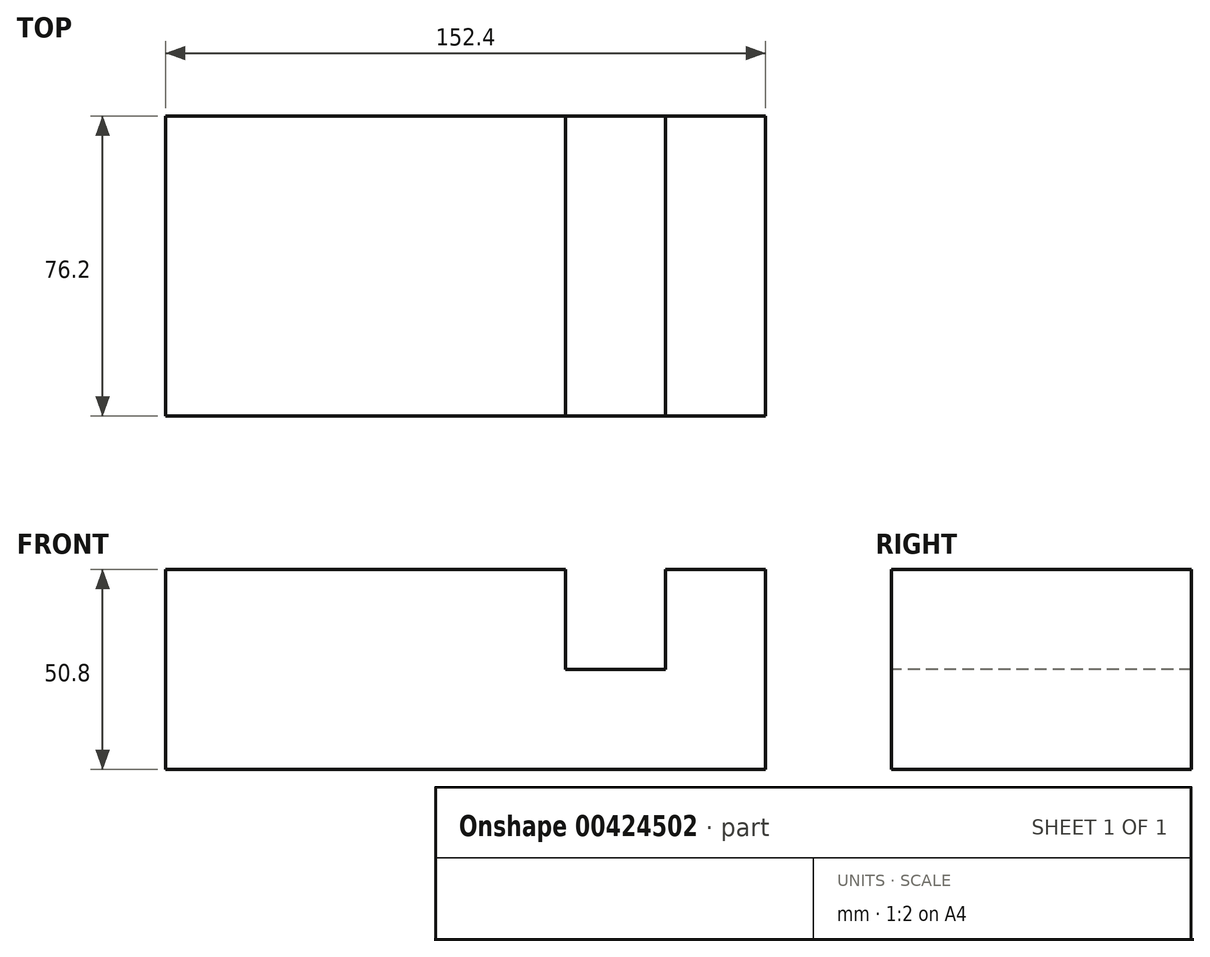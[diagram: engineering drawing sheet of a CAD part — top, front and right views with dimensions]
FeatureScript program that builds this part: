
annotation { "Feature Type Name" : "Feature", "Feature Type Description" : "" }
export const myFeature = defineFeature(function(context is Context, id is Id, definition is map)
    precondition{}
    {
        {
            var Q0;
            Q0=qCreatedBy(makeId("Front.planeOp"),FACE);
            var sketch = newSketch(context, id + "F0", { "sketchPlane" : qUnion([Q0])});
            skLineSegment(sketch, "E0", {"start": v(0, 0) * mm, "end": v(152.4, 0) * mm});
            skLineSegment(sketch, "E1", {"start": v(152.4, 0) * mm, "end": v(152.4, 50.8) * mm});
            skLineSegment(sketch, "E2", {"start": v(152.4, 50.8) * mm, "end": v(127, 50.8) * mm});
            skLineSegment(sketch, "E3", {"start": v(127, 50.8) * mm, "end": v(127, 25.4) * mm});
            skLineSegment(sketch, "E4", {"start": v(127, 25.4) * mm, "end": v(101.6, 25.4) * mm});
            skLineSegment(sketch, "E5", {"start": v(101.6, 25.4) * mm, "end": v(101.6, 50.8) * mm});
            skLineSegment(sketch, "E6", {"start": v(101.6, 50.8) * mm, "end": v(0, 50.8) * mm});
            skLineSegment(sketch, "E7", {"start": v(0, 50.8) * mm, "end": v(0, 0) * mm});
            skSolve(sketch);
        }
        {
            var Q0;
            Q0 = qSketchRegion(id + "F0", true);
            extrude(context, id + "F1", {"entities" : qUnion([Q0]), "oppositeDirection" : true, "depth" : 76.2 * mm});
        }
    });
